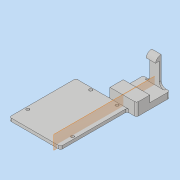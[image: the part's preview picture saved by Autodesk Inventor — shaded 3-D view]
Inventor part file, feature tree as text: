
AUTODESK INVENTOR PART (.ipt)
format: ipt  version: 2017 (Build 210142000, 142)  size: 179,200 bytes
history: native  units: in
note: dims shown in document units (in); Inventor stores cm internally (conversion verified against a paired STEP export)
features: extrude x5, sketch x5, fillet x2, plane x1
ambient origin geometry x8: Origin, YZ Plane, XZ Plane, XY Plane, X Axis, Y Axis, Z Axis, Center Point
bodies: Solid1 (feature_tree)
feature tree (13):
  extrude  "Extrusion1"  Depth=2.7559in
  extrude  "Extrusion2"  Depth=0.3937in
  extrude  "Extrusion3"  Depth=0.125in TaperAngle=0.0deg
  plane  "Work Plane1"
  extrude  "Extrusion4"  Depth=0.1181in TaperAngle=0.0deg
  extrude  "Extrusion5"  Depth=0.0787in
  fillet  "Fillet1"  Radius=1.1417in
  fillet  "Fillet2"  Radius=0.9449in
  sketch  "Sketch1"  dims[d0=2.126in d1=2.7559in]
  sketch  "Sketch2"  dims[d2=1.1024in d3=0.3937in]
  sketch  "Sketch3"  dims[d4=1.378in d5=0.125in d6=0.0in]
  sketch  "Sketch4"  dims[d7=0.5512in d8=0.1181in d9=0.0in]
  sketch  "Sketch5"  dims[d10=0.3937in d11=0.0in d12=0.0787in d13=1.1417in d14=0.9449in d15=0.1575in d16=0.3937in d17=0.0in d18=0.3937in d19=0.0in d20=0.0787in d21=0.0787in d22=0.1969in]
